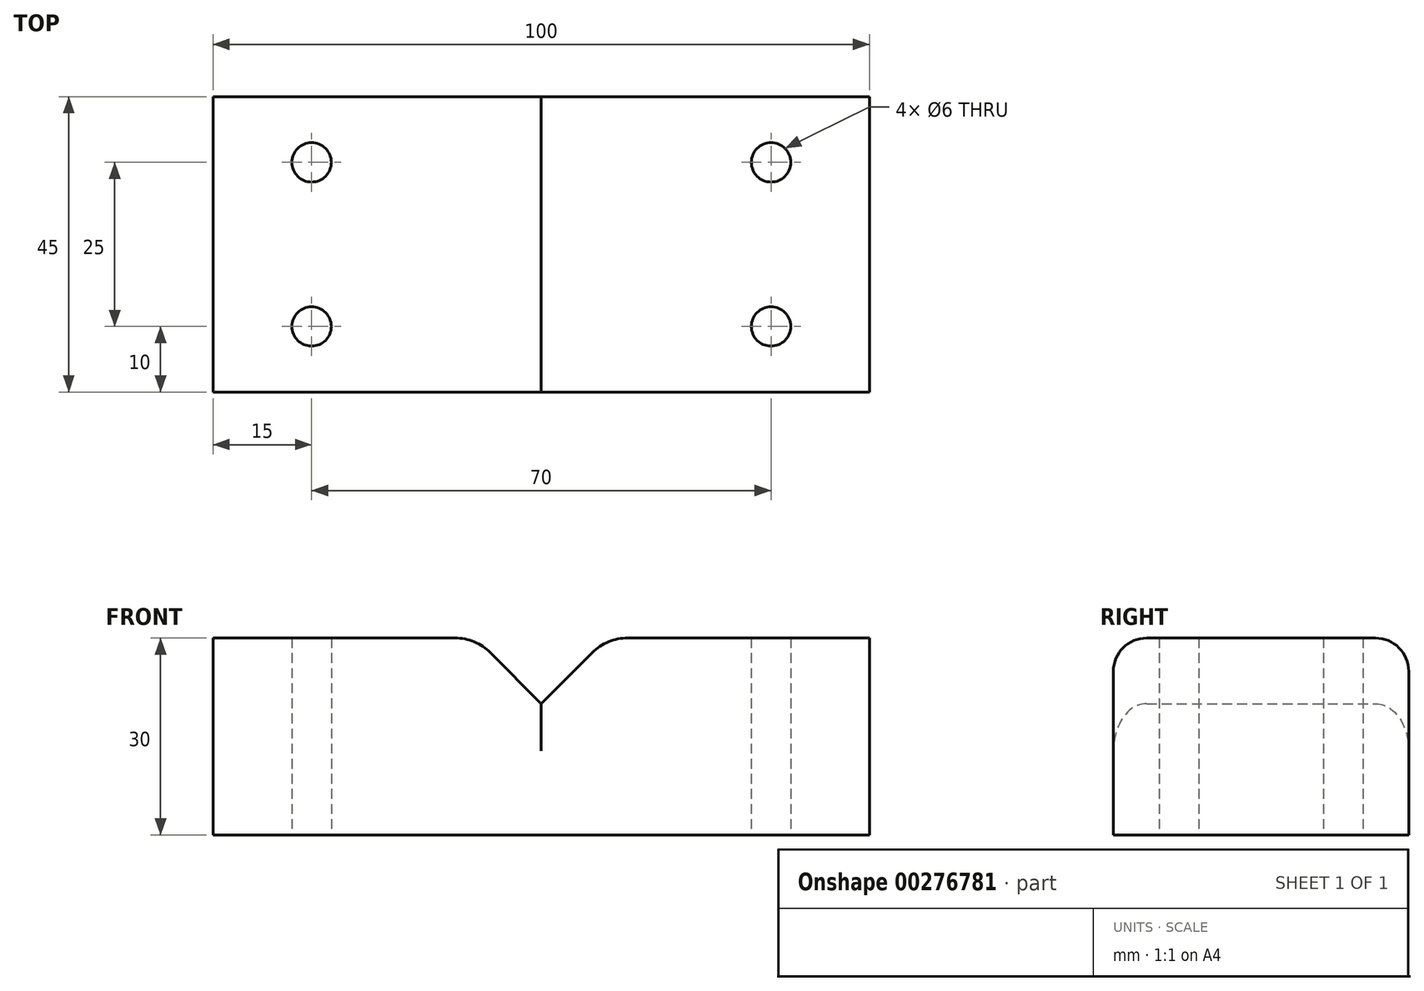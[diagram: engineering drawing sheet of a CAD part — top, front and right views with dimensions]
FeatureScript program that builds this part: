
annotation { "Feature Type Name" : "Feature", "Feature Type Description" : "" }
export const myFeature = defineFeature(function(context is Context, id is Id, definition is map)
    precondition{}
    {
        {
            var Q0;
            Q0=qCreatedBy(makeId("Front.planeOp"),FACE);
            var sketch = newSketch(context, id + "F0", { "sketchPlane" : qUnion([Q0])});
            skPoint(sketch, "E0.middle", {"position": v(0, 0) * mm});
            skLineSegment(sketch, "E1", {"start": v(20, 20) * mm, "end": v(50, 20) * mm});
            skLineSegment(sketch, "E2", {"start": v(50, 20) * mm, "end": v(50, 0) * mm});
            skLineSegment(sketch, "E3", {"start": v(-20, 20) * mm, "end": v(-50, 20) * mm});
            skLineSegment(sketch, "E4", {"start": v(-50, 20) * mm, "end": v(-50, 0) * mm});
            skLineSegment(sketch, "E5", {"start": v(-50, 0) * mm, "end": v(-50, -10) * mm});
            skLineSegment(sketch, "E6", {"start": v(-50, -10) * mm, "end": v(50, -10) * mm});
            skLineSegment(sketch, "E7", {"start": v(50, -10) * mm, "end": v(50, 0) * mm});
            skLineSegment(sketch, "E8", {"start": v(-20, 20) * mm, "end": v(-10, 20) * mm});
            skLineSegment(sketch, "E9", {"start": v(20, 20) * mm, "end": v(10, 20) * mm});
            skLineSegment(sketch, "E10", {"start": v(-10, 20) * mm, "end": v(0, 10) * mm});
            skLineSegment(sketch, "E11", {"start": v(0, 10) * mm, "end": v(10, 20) * mm});
            skSolve(sketch);
        }
        {
            var Q0;
            Q0=qSketchRegion(id+"F0",true);
            extrude(context, id + "F1", {"entities" : qUnion([Q0]), "depth" : 45 * mm});
        }
        {
            var Q0;
            Q0=makeQuery(id+"F1.opExtrude","SWEPT_EDGE",EDGE,{"disambiguationData":[OSD([sQuery(id+"F0.wireOp",EDGE,"E9"),sQuery(id+"F0.wireOp",EDGE,"E11")])]});
            var Q1;
            Q1=makeQuery(id+"F1.opExtrude","SWEPT_EDGE",EDGE,{"disambiguationData":[OSD([sQuery(id+"F0.wireOp",EDGE,"E8"),sQuery(id+"F0.wireOp",EDGE,"E10")])]});
            fillet(context, id + "F2", {"entities" : qUnion([Q0, Q1]), "radius" : 7.62 * mm, "tangentPropagation" : true, "allowEdgeOverflow" : false});
        }
        {
            var Q0;
            Q0=makeQuery(id+"F1.opExtrude","CAP_EDGE",EDGE,{"disambiguationData":[OSD([sQuery(id+"F0.wireOp",EDGE,"E3"),sQuery(id+"F0.wireOp",EDGE,"E8")])],"isStart":false});
            var Q1;
            Q1=makeQuery(id+"F1.opExtrude","CAP_EDGE",EDGE,{"disambiguationData":[OSD([sQuery(id+"F0.wireOp",EDGE,"E1"),sQuery(id+"F0.wireOp",EDGE,"E9")])],"isStart":false});
            var Q2;
            Q2=makeQuery(id+"F1.opExtrude","CAP_EDGE",EDGE,{"disambiguationData":[OSD([sQuery(id+"F0.wireOp",EDGE,"E1"),sQuery(id+"F0.wireOp",EDGE,"E9")])],"isStart":true});
            var Q3;
            Q3=makeQuery(id+"F1.opExtrude","CAP_EDGE",EDGE,{"disambiguationData":[OSD([sQuery(id+"F0.wireOp",EDGE,"E3"),sQuery(id+"F0.wireOp",EDGE,"E8")])],"isStart":true});
            fillet(context, id + "F3", {"entities" : qUnion([Q0, Q1, Q2, Q3]), "radius" : 5.08 * mm, "tangentPropagation" : true, "allowEdgeOverflow" : false});
        }
        {
            var Q0;
            Q0=makeQuery(id+"F1.opExtrude","SWEPT_FACE",FACE,{"disambiguationData":[OSD([sQuery(id+"F0.wireOp",EDGE,"E6")])]});
            var sketch = newSketch(context, id + "F4", { "sketchPlane" : qUnion([Q0])});
            skCircle(sketch, "E12", {"center": v(35, 35) * mm, "radius": 3 * mm});
            skCircle(sketch, "E13", {"center": v(35, 10) * mm, "radius": 3 * mm});
            skCircle(sketch, "E14", {"center": v(-35, 10) * mm, "radius": 3 * mm});
            skCircle(sketch, "E15", {"center": v(-35, 35) * mm, "radius": 3 * mm});
            skSolve(sketch);
        }
        {
            var Q0;
            Q0=sQuery(id+"F4.wireOp",VERTEX,"E13.center");
            var Q1;
            Q1=sQuery(id+"F4.wireOp",VERTEX,"E12.center");
            var Q2;
            Q2=sQuery(id+"F4.wireOp",VERTEX,"E15.center");
            var Q3;
            Q3=sQuery(id+"F4.wireOp",VERTEX,"E14.center");
            var Q4;
            Q4=makeQuery(id+"F1.opExtrude","SWEPT_BODY",BODY,{"disambiguationData":[OSD([sQuery(id+"F0.wireOp",EDGE,"E1"),sQuery(id+"F0.wireOp",EDGE,"E2"),sQuery(id+"F0.wireOp",EDGE,"E3"),sQuery(id+"F0.wireOp",EDGE,"E4"),sQuery(id+"F0.wireOp",EDGE,"E5"),sQuery(id+"F0.wireOp",EDGE,"E6"),sQuery(id+"F0.wireOp",EDGE,"E7"),sQuery(id+"F0.wireOp",EDGE,"E8"),sQuery(id+"F0.wireOp",EDGE,"E9"),sQuery(id+"F0.wireOp",EDGE,"E10"),sQuery(id+"F0.wireOp",EDGE,"E11")])]});
            hole(context, id + "F5", {"style" : HoleStyle.SIMPLE, "endStyle" : HoleEndStyle.THROUGH, "holeDiameter" : 6 * mm, "tappedDepth" : 12.7 * mm, "tapClearance" : 3, "locations" : qUnion([Q0, Q1, Q2, Q3]), "scope" : qUnion([Q4])});
        }
    });
